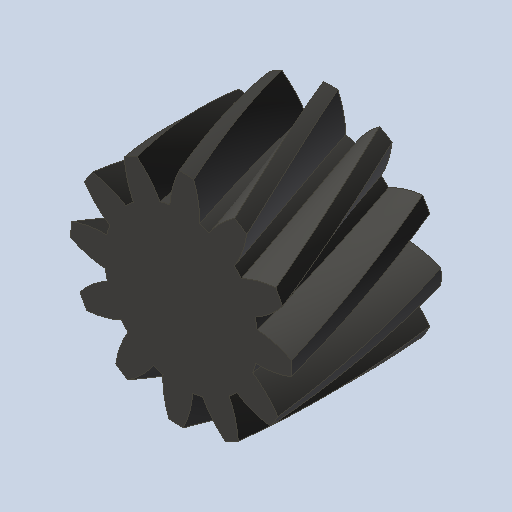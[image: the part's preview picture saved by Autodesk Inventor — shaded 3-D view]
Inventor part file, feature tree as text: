
AUTODESK INVENTOR PART (.ipt)
format: ipt  version: 2023 (Build 270158000, 158)  size: 333,312 bytes
history: native  units: mm (DEFAULTED — no unit token found)
features: plane x3, other x3, sketch x2, extrude x1
ambient origin geometry x8: Origin, YZ Plane, XZ Plane, XY Plane, X Axis, Y Axis, Z Axis, Center Point
bodies: Solid1 (feature_tree)
feature tree (9):
  extrude  "Extrusion1"  Depth=10.0mm TaperAngle=0.0deg
  plane  "Work Plane2"
  plane  "Work Plane8"
  plane  "Work Plane9"
  other  "Spur Gear"
  sketch  "Sketch1"  dims[d0=14.770133mm d1=10.0mm d2=0.0mm]
  sketch  "Sketch2"  dims[d3=12.770133mm d4=10.0mm d5=0.0mm d16=50.0mm d17=0.0mm d34=15.0deg d39=0.0mm d41=0.0mm d43=50.0mm d46=50.0mm d47=0.0mm d48=0.0mm]
  other  "Srf1"
  other  "Pitch Diameter"
